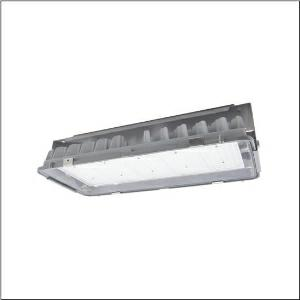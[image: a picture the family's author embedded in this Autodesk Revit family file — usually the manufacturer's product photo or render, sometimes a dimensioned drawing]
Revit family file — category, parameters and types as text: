
# Revit family: highbay_11xtreme_51hf81da4nma
name_source: partatom
category: Lighting Fixtures
units: mm (PartAtom-declared; Revit-internal decimal feet)

## family parameters
Cut with Voids When Loaded = No
Host = Face
Light Source = No
Part Type = Normal
Room Calculation Point = No
Round Connector Dimension = Use Diameter
Shared = No

## types (1)
- --- (1 x LED, 34200 lm, 188.1 W, 4000K)
    Apparent Load = 188 VA
    CIE Flux Codes = 88 96 99 100 100
    Color Rendering = 80
    Color Temperature = 4000K
    Default Elevation = 1800 mm
    Description = Highbay 11Xtreme, high bay luminaire, primary light control with lens, of PMMA, primary optical cover: cover, of toughened safety glass, light emission: direct distribution, primary light characteristic: symmetric, installation type: suspended mounting, surface-mounted, 1x LED module,for 1x LED, rated luminous flux: 34.200lm, luminous efficacy: 182lm/W, light colour: 840, colour temperature: 4000K, control gear: DALI 2, with cable H07RN-F 5x 1.5mm², mains connection: 220..240V, AC, 50/60Hz, cable length: 1,5m, rated input power: 188W, luminaire housing, of diecast aluminium, partly coated, silver, length: 595mm, width: 280mm, height: 195mm, protection rating (complete): IP66, insulation class (complete): insulation class I (protective earthing), certification: CE, ENEC, UKCA, protection symbol: D, ball protection: ball impact resistant according to DIN VDE 0710 part 13 (with chain suspension), impact resistance: IK08, permissible operating ambient temperature: -25..+45°C, reducing of maximum allowable ambient temperature of 5°C with ceiling mounting, packaging unit: 1 piece
    Height = 157 mm
    Lamp = 1 x LED
    Lamp Light Flux = 34200 lm
    Lamp Power = 188.1 W
    Lamp count = 1
    Length = 593 mm
    Luminous efficacy = 182 lm/W
    Manufacturer = Siteco
    ModVariant = No
    Model = 51HF81DA4NMA
    Mounting Place = Ceiling
    Mounting Type = Pendant
    Number of Poles = 1
    OnlyDefault = Yes
    Power Factor = 1
    Product Name = Highbay 11Xtreme
    Product group = high bay luminaire
    ProductGroupID = 902
    Protection Class = Protection class I
    Protection Degree = IP 66
    RLX_Detail_Level = 1
    RLX_Emergency_Light_Flux = 0 lm
    RLX_Emergency_Type = 0
    RLX_Emergency_Type_DB = No
    RlxData = <blob elided: 27853 chars, md5=3878598a>
    Socket = socket
    Standby Power = 0 W
    System Light Flux = 34200 lm
    System Power = 188 W
    Type Comments = factory setting: luminous flux: 100 % | dim-lin: 254 | 1258 mA
    Type Image = l_1258342.jpg
    URL = http://relux.com
    VarID = @adj_088701
    Voltage = 0 V
    Weight = 0.00 kg
    Width = 278 mm

## geometry (parser evidence)
native form markers: Blend x4, Sweep x10
no freeform markers — native parametric forms only
